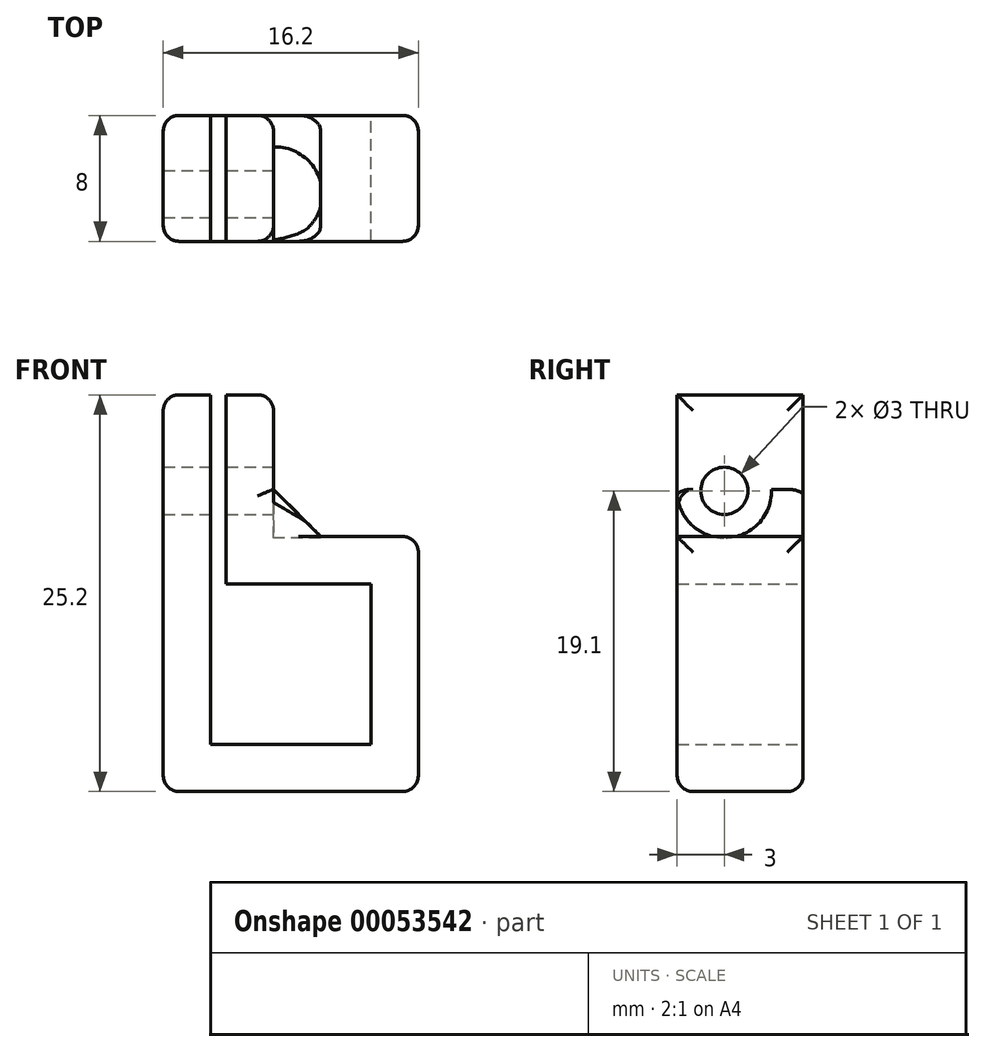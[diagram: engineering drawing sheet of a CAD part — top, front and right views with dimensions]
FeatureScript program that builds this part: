
annotation { "Feature Type Name" : "Feature", "Feature Type Description" : "" }
export const myFeature = defineFeature(function(context is Context, id is Id, definition is map)
    precondition{}
    {
        {
            var Q0;
            Q0=qCreatedBy(makeId("Front.planeOp"),FACE);
            var sketch = newSketch(context, id + "F0", { "sketchPlane" : qUnion([Q0])});
            skLineSegment(sketch, "E0.rect.bottom", {"start": v(5.1, -5.1) * mm, "end": v(-5.1, -5.1) * mm});
            skLineSegment(sketch, "E0.rect.top", {"start": v(5.1, 5.1) * mm, "end": v(-4.1, 5.1) * mm});
            skLineSegment(sketch, "E0.rect.left", {"start": v(5.1, -5.1) * mm, "end": v(5.1, 5.1) * mm});
            skLineSegment(sketch, "E0.rect.right", {"start": v(-5.1, -5.1) * mm, "end": v(-5.1, 5.1) * mm});
            skPoint(sketch, "E0.rect.middle", {"position": v(0, 0) * mm});
            skLineSegment(sketch, "E1.0", {"start": v(8.1, 8.1) * mm, "end": v(-1.1, 8.1) * mm});
            skLineSegment(sketch, "E1.1", {"start": v(8.1, -8.1) * mm, "end": v(8.1, 8.1) * mm});
            skLineSegment(sketch, "E1.2", {"start": v(8.1, -8.1) * mm, "end": v(-8.1, -8.1) * mm});
            skLineSegment(sketch, "E1.3", {"start": v(-8.1, -8.1) * mm, "end": v(-8.1, 8.1) * mm});
            skLineSegment(sketch, "E2", {"start": v(-8.1, 8.1) * mm, "end": v(-8.1, 17.1) * mm});
            skLineSegment(sketch, "E3", {"start": v(-8.1, 17.1) * mm, "end": v(-5.1, 17.1) * mm});
            skLineSegment(sketch, "E4", {"start": v(-5.1, 17.1) * mm, "end": v(-5.1, 8.1) * mm});
            skLineSegment(sketch, "E5", {"start": v(-4.1, 8.1) * mm, "end": v(-4.1, 17.1) * mm});
            skLineSegment(sketch, "E6", {"start": v(-4.1, 17.1) * mm, "end": v(-1.1, 17.1) * mm});
            skLineSegment(sketch, "E7", {"start": v(-1.1, 17.1) * mm, "end": v(-1.1, 8.1) * mm});
            skLineSegment(sketch, "E8", {"start": v(-5.1, 5.1) * mm, "end": v(-5.1, 8.1) * mm});
            skLineSegment(sketch, "E9", {"start": v(-4.1, 8.1) * mm, "end": v(-4.1, 5.1) * mm});
            skSolve(sketch);
        }
        {
            var Q0;
            Q0 = qSketchRegion(id + "F0", true);
            extrude(context, id + "F1", {"entities" : qUnion([Q0]), "depth" : 8 * mm});
        }
        {
            var Q0;
            Q0=makeQuery(id+"F1.opExtrude","SWEPT_FACE",FACE,{"disambiguationData":[OSD([sQuery(id+"F0.wireOp",EDGE,"E7")])]});
            var sketch = newSketch(context, id + "F2", { "sketchPlane" : qUnion([Q0])});
            skCircle(sketch, "E10", {"center": v(-5, 11) * mm, "radius": 1.5 * mm});
            skPoint(sketch, "E10.centerSnap0", {"position": v(-9, 11) * mm});
            skPoint(sketch, "E10.centerSnap1", {"position": v(-5, 15.5) * mm});
            skSolve(sketch);
        }
        {
            var Q0;
            Q0 = qSketchRegion(id + "F2", true);
            extrude(context, id + "F3", {"entities" : qUnion([Q0]), "operationType" : NewBodyOperationType.REMOVE, "endBound" : BoundingType.THROUGH_ALL, "oppositeDirection" : true, "depth" : 25 * mm});
        }
        {
            var Q0;
            Q0=makeQuery(id+"F1.opExtrude","SWEPT_EDGE",EDGE,{"disambiguationData":[OSD([sQuery(id+"F0.wireOp",EDGE,"E1.0"),sQuery(id+"F0.wireOp",EDGE,"E7")])]});
            chamfer(context, id + "F4", {"entities" : qUnion([Q0]), "width" : 3 * mm, "tangentPropagation" : true});
        }
        {
            var Q0;
            Q0=makeQuery(id+"F1.opExtrude","SWEPT_FACE",FACE,{"disambiguationData":[OSD([sQuery(id+"F0.wireOp",EDGE,"E1.1")])]});
            var Q1;
            Q1=makeQuery(id+"F1.opExtrude","SWEPT_FACE",FACE,{"disambiguationData":[OSD([sQuery(id+"F0.wireOp",EDGE,"E1.2")])]});
            var Q2;
            Q2=makeQuery(id+"F1.opExtrude","SWEPT_EDGE",EDGE,{"disambiguationData":[OSD([sQuery(id+"F0.wireOp",EDGE,"E2"),sQuery(id+"F0.wireOp",EDGE,"E3")])]});
            var Q3;
            Q3=makeQuery(id+"F1.opExtrude","CAP_EDGE",EDGE,{"disambiguationData":[OSD([sQuery(id+"F0.wireOp",EDGE,"E1.3"),sQuery(id+"F0.wireOp",EDGE,"E2")])],"isStart":true});
            var Q4;
            Q4=makeQuery(id+"F1.opExtrude","CAP_EDGE",EDGE,{"disambiguationData":[OSD([sQuery(id+"F0.wireOp",EDGE,"E1.3"),sQuery(id+"F0.wireOp",EDGE,"E2")])],"isStart":false});
            var Q5;
            Q5=makeQuery(id+"F1.opExtrude","SWEPT_EDGE",EDGE,{"disambiguationData":[OSD([sQuery(id+"F0.wireOp",EDGE,"E6"),sQuery(id+"F0.wireOp",EDGE,"E7")])]});
            var Q6;
            Q6=makeQuery(id+"F1.opExtrude","CAP_EDGE",EDGE,{"disambiguationData":[OSD([sQuery(id+"F0.wireOp",EDGE,"E7")])],"isStart":true});
            var Q7;
            Q7=makeQuery(id+"F1.opExtrude","CAP_EDGE",EDGE,{"disambiguationData":[OSD([sQuery(id+"F0.wireOp",EDGE,"E7")])],"isStart":false});
            fillet(context, id + "F5", {"entities" : qUnion([Q0, Q1, Q2, Q3, Q4, Q5, Q6, Q7]), "radius" : 1 * mm, "tangentPropagation" : true, "allowEdgeOverflow" : false});
        }
        {
            var Q0;
            {var subQ0=sQuery(id+"F0.wireOp",EDGE,"E7");var subQ1=sQuery(id+"F0.wireOp",EDGE,"E1.0");Q0=makeQuery(id+"F4.opChamfer","BLEND_EDGE",EDGE,{"blendedFrom":[makeQuery(id+"F1.opExtrude","SWEPT_EDGE",EDGE,{"disambiguationData":[OSD([subQ1,subQ0])]}),makeQuery(id+"F1.opExtrude","CAP_FACE",FACE,{"disambiguationData":[OSD([sQuery(id+"F0.wireOp",EDGE,"E0.rect.bottom"),sQuery(id+"F0.wireOp",EDGE,"E0.rect.top"),sQuery(id+"F0.wireOp",EDGE,"E0.rect.left"),sQuery(id+"F0.wireOp",EDGE,"E0.rect.right"),subQ1,sQuery(id+"F0.wireOp",EDGE,"E1.1"),sQuery(id+"F0.wireOp",EDGE,"E1.2"),sQuery(id+"F0.wireOp",EDGE,"E1.3"),sQuery(id+"F0.wireOp",EDGE,"E2"),sQuery(id+"F0.wireOp",EDGE,"E3"),sQuery(id+"F0.wireOp",EDGE,"E4"),sQuery(id+"F0.wireOp",EDGE,"E5"),sQuery(id+"F0.wireOp",EDGE,"E6"),subQ0,sQuery(id+"F0.wireOp",EDGE,"E8"),sQuery(id+"F0.wireOp",EDGE,"E9")])],"isStart":true})],"blendedInto":[makeQuery(id+"F1.opExtrude","CAP_FACE",FACE,{"disambiguationData":[OSD([sQuery(id+"F0.wireOp",EDGE,"E0.rect.bottom"),sQuery(id+"F0.wireOp",EDGE,"E0.rect.top"),sQuery(id+"F0.wireOp",EDGE,"E0.rect.left"),sQuery(id+"F0.wireOp",EDGE,"E0.rect.right"),subQ1,sQuery(id+"F0.wireOp",EDGE,"E1.1"),sQuery(id+"F0.wireOp",EDGE,"E1.2"),sQuery(id+"F0.wireOp",EDGE,"E1.3"),sQuery(id+"F0.wireOp",EDGE,"E2"),sQuery(id+"F0.wireOp",EDGE,"E3"),sQuery(id+"F0.wireOp",EDGE,"E4"),sQuery(id+"F0.wireOp",EDGE,"E5"),sQuery(id+"F0.wireOp",EDGE,"E6"),subQ0,sQuery(id+"F0.wireOp",EDGE,"E8"),sQuery(id+"F0.wireOp",EDGE,"E9")])],"isStart":true})]});}
            var Q1;
            {var subQ0=sQuery(id+"F0.wireOp",EDGE,"E7");var subQ1=sQuery(id+"F0.wireOp",EDGE,"E1.0");Q1=makeQuery(id+"F4.opChamfer","BLEND_EDGE",EDGE,{"blendedFrom":[makeQuery(id+"F1.opExtrude","SWEPT_EDGE",EDGE,{"disambiguationData":[OSD([subQ1,subQ0])]}),makeQuery(id+"F1.opExtrude","CAP_FACE",FACE,{"disambiguationData":[OSD([sQuery(id+"F0.wireOp",EDGE,"E0.rect.bottom"),sQuery(id+"F0.wireOp",EDGE,"E0.rect.top"),sQuery(id+"F0.wireOp",EDGE,"E0.rect.left"),sQuery(id+"F0.wireOp",EDGE,"E0.rect.right"),subQ1,sQuery(id+"F0.wireOp",EDGE,"E1.1"),sQuery(id+"F0.wireOp",EDGE,"E1.2"),sQuery(id+"F0.wireOp",EDGE,"E1.3"),sQuery(id+"F0.wireOp",EDGE,"E2"),sQuery(id+"F0.wireOp",EDGE,"E3"),sQuery(id+"F0.wireOp",EDGE,"E4"),sQuery(id+"F0.wireOp",EDGE,"E5"),sQuery(id+"F0.wireOp",EDGE,"E6"),subQ0,sQuery(id+"F0.wireOp",EDGE,"E8"),sQuery(id+"F0.wireOp",EDGE,"E9")])],"isStart":false})],"blendedInto":[makeQuery(id+"F1.opExtrude","CAP_FACE",FACE,{"disambiguationData":[OSD([sQuery(id+"F0.wireOp",EDGE,"E0.rect.bottom"),sQuery(id+"F0.wireOp",EDGE,"E0.rect.top"),sQuery(id+"F0.wireOp",EDGE,"E0.rect.left"),sQuery(id+"F0.wireOp",EDGE,"E0.rect.right"),subQ1,sQuery(id+"F0.wireOp",EDGE,"E1.1"),sQuery(id+"F0.wireOp",EDGE,"E1.2"),sQuery(id+"F0.wireOp",EDGE,"E1.3"),sQuery(id+"F0.wireOp",EDGE,"E2"),sQuery(id+"F0.wireOp",EDGE,"E3"),sQuery(id+"F0.wireOp",EDGE,"E4"),sQuery(id+"F0.wireOp",EDGE,"E5"),sQuery(id+"F0.wireOp",EDGE,"E6"),subQ0,sQuery(id+"F0.wireOp",EDGE,"E8"),sQuery(id+"F0.wireOp",EDGE,"E9")])],"isStart":false})]});}
            fillet(context, id + "F6", {"entities" : qUnion([Q0, Q1]), "radius" : 1 * mm, "tangentPropagation" : true, "allowEdgeOverflow" : false});
        }
        {
            var Q0;
            Q0=makeQuery(id+"F1.opExtrude","SWEPT_FACE",FACE,{"disambiguationData":[OSD([sQuery(id+"F0.wireOp",EDGE,"E7")])]});
            var sketch = newSketch(context, id + "F7", { "sketchPlane" : qUnion([Q0])});
            skCircle(sketch, "E11", {"center": v(-5, 11) * mm, "radius": 3 * mm});
            skSolve(sketch);
        }
        {
            var Q0;
            Q0 = qSketchRegion(id + "F7", true);
            extrude(context, id + "F8", {"entities" : qUnion([Q0]), "operationType" : NewBodyOperationType.REMOVE, "depth" : 3 * mm});
        }
    });
